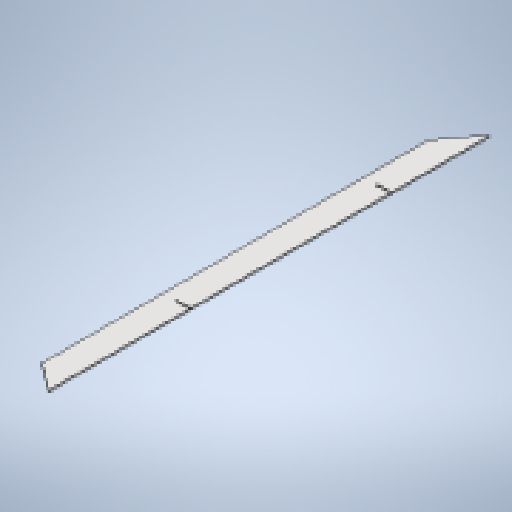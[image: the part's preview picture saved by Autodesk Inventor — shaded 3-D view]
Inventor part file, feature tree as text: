
AUTODESK INVENTOR PART (.ipt)
format: ipt  version: 2025 (Build 290162010, 162A)  size: 207,872 bytes
history: native  units: mm
features: other x3, chamfer x2, sketch x2, sheet_metal_op x1, extrude x1, pattern_linear x1
ambient origin geometry x8: Origin, YZ Plane, XZ Plane, XY Plane, X Axis, Y Axis, Z Axis, Center Point
bodies: Solid1 (feature_tree)
feature tree (10):
  sheet_metal_op  "Face1"
  other  "Corner Chamfer2"
  chamfer  "Corner Round1"
  extrude  "Extrusion1"  Depth=50.0mm
  pattern_linear  "Rectangular Pattern1"  Spacing1=9.372418mm  [1 undecoded]
  chamfer  "Corner Round3"
  sketch  "Sketch1"  dims[d0=50.0mm d1=860.0mm]
  other  "Plate1"
  sketch  "Sketch2"  dims[d2=3.0mm d5=9.372418mm d6=9.372418mm d10=3.0mm d11=6.0mm d12=45.0deg d13=6.0mm d15=188.0mm d16=26.0mm d17=3.0mm d18=0.0mm d19=0.0mm d20=30.0mm d22=323.0mm d23=6.0mm]
  other  "Definition1"
note: 1 required parameter value undecoded (feature->parameter linkage not recoverable at this tier; creation-order binding heuristic only, values carry confidence <= 0.55)
